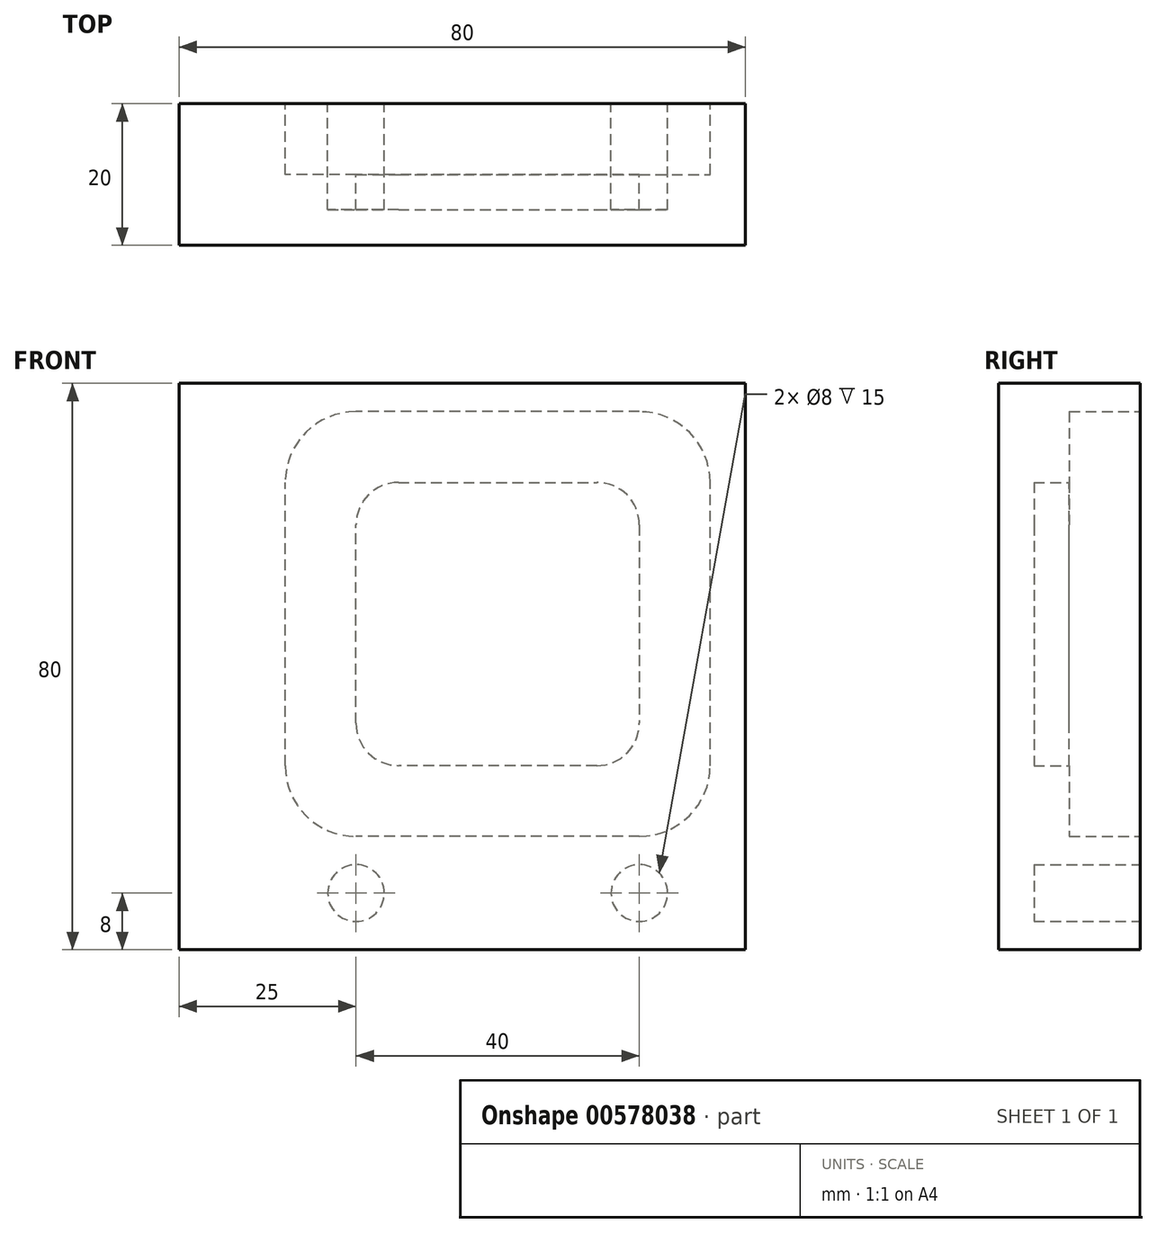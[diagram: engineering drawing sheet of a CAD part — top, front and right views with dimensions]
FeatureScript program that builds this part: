
annotation { "Feature Type Name" : "Feature", "Feature Type Description" : "" }
export const myFeature = defineFeature(function(context is Context, id is Id, definition is map)
    precondition{}
    {
        {
            var Q0;
            Q0=qCreatedBy(makeId("Front.planeOp"),FACE);
            var sketch = newSketch(context, id + "F0", { "sketchPlane" : qUnion([Q0])});
            skLineSegment(sketch, "E0", {"start": v(0, 0) * mm, "end": v(80, 0) * mm});
            skLineSegment(sketch, "E1", {"start": v(80, 0) * mm, "end": v(80, -80) * mm});
            skLineSegment(sketch, "E2", {"start": v(80, -80) * mm, "end": v(0, -80) * mm});
            skLineSegment(sketch, "E3", {"start": v(0, -80) * mm, "end": v(0, 0) * mm});
            skSolve(sketch);
        }
        {
            var Q0;
            Q0=makeQuery(id+"F0.imprint","IMPRINT",FACE,{"disambiguationData":[TD([[makeQuery(id+"F0.imprint","IMPRINT",EDGE,{"derivedFrom":sQuery(id+"F0.wireOp",EDGE,"E0")}),-1.0]])]});
            extrude(context, id + "F1", {"entities" : qUnion([Q0]), "depth" : 20 * mm, "offsetDistance" : 25 * mm});
        }
        {
            var Q0;
            Q0=makeQuery(id+"F1.opExtrude","CAP_FACE",FACE,{"disambiguationData":[OSD([sQuery(id+"F0.wireOp",EDGE,"E0"),sQuery(id+"F0.wireOp",EDGE,"E1"),sQuery(id+"F0.wireOp",EDGE,"E2"),sQuery(id+"F0.wireOp",EDGE,"E3")])],"isStart":true});
            var sketch = newSketch(context, id + "F2", { "sketchPlane" : qUnion([Q0])});
            skLineSegment(sketch, "E4", {"start": v(-59, -54) * mm, "end": v(-31, -54) * mm});
            skLineSegment(sketch, "E5", {"start": v(-25, -48) * mm, "end": v(-25, -20) * mm});
            skLineSegment(sketch, "E6", {"start": v(-31, -14) * mm, "end": v(-59, -14) * mm});
            skLineSegment(sketch, "E7", {"start": v(-65, -20) * mm, "end": v(-65, -48) * mm});
            skArc(sketch, "E8", {"start": v(-65, -48) * mm, "mid": v(-63.24, -52.24) * mm, "end": v(-59, -54) * mm});
            skArc(sketch, "E9", {"start": v(-59, -14) * mm, "mid": v(-63.24, -15.76) * mm, "end": v(-65, -20) * mm});
            skArc(sketch, "E10", {"start": v(-25, -20) * mm, "mid": v(-26.76, -15.76) * mm, "end": v(-31, -14) * mm});
            skArc(sketch, "E11", {"start": v(-31, -54) * mm, "mid": v(-26.76, -52.24) * mm, "end": v(-25, -48) * mm});
            skLineSegment(sketch, "E12", {"start": v(-75, -54) * mm, "end": v(-75, -14) * mm});
            skLineSegment(sketch, "E13", {"start": v(-65, -4) * mm, "end": v(-25, -4) * mm});
            skLineSegment(sketch, "E14", {"start": v(-65, -64) * mm, "end": v(-25, -64) * mm});
            skLineSegment(sketch, "E15", {"start": v(-15, -54) * mm, "end": v(-15, -14) * mm});
            skArc(sketch, "E16", {"start": v(-75, -54) * mm, "mid": v(-72.07, -61.07) * mm, "end": v(-65, -64) * mm});
            skArc(sketch, "E17", {"start": v(-65, -4) * mm, "mid": v(-72.07, -6.93) * mm, "end": v(-75, -14) * mm});
            skArc(sketch, "E18", {"start": v(-15, -14) * mm, "mid": v(-17.93, -6.93) * mm, "end": v(-25, -4) * mm});
            skArc(sketch, "E19", {"start": v(-25, -64) * mm, "mid": v(-17.93, -61.07) * mm, "end": v(-15, -54) * mm});
            skCircle(sketch, "E20", {"center": v(-65, -72) * mm, "radius": 4 * mm});
            skCircle(sketch, "E21", {"center": v(-25, -72) * mm, "radius": 4 * mm});
            skSolve(sketch);
        }
        {
            var Q0;
            Q0=makeQuery(id+"F2.imprint","IMPRINT",FACE,{"disambiguationData":[TD([[makeQuery(id+"F2.imprint","IMPRINT",EDGE,{"derivedFrom":sQuery(id+"F2.wireOp",EDGE,"E20")}),1.0]])]});
            var Q1;
            Q1=makeQuery(id+"F2.imprint","IMPRINT",FACE,{"disambiguationData":[TD([[makeQuery(id+"F2.imprint","IMPRINT",EDGE,{"derivedFrom":sQuery(id+"F2.wireOp",EDGE,"E21")}),1.0]])]});
            extrude(context, id + "F3", {"entities" : qUnion([Q0, Q1]), "operationType" : NewBodyOperationType.REMOVE, "oppositeDirection" : true, "depth" : 15 * mm, "offsetDistance" : 25 * mm});
        }
        {
            var Q0;
            Q0=makeQuery(id+"F2.imprint","IMPRINT",FACE,{"disambiguationData":[TD([[makeQuery(id+"F2.imprint","IMPRINT",EDGE,{"derivedFrom":sQuery(id+"F2.wireOp",EDGE,"E4")}),1.0]])]});
            extrude(context, id + "F4", {"entities" : qUnion([Q0]), "operationType" : NewBodyOperationType.REMOVE, "oppositeDirection" : true, "depth" : 15 * mm, "offsetDistance" : 25 * mm});
        }
        {
            var Q0;
            Q0=makeQuery(id+"F2.imprint","IMPRINT",FACE,{"disambiguationData":[TD([[makeQuery(id+"F2.imprint","IMPRINT",EDGE,{"derivedFrom":sQuery(id+"F2.wireOp",EDGE,"E4")}),-1.0]])]});
            extrude(context, id + "F5", {"entities" : qUnion([Q0]), "operationType" : NewBodyOperationType.REMOVE, "oppositeDirection" : true, "depth" : 10 * mm, "offsetDistance" : 25 * mm});
        }
    });
